# Revit family: Andreu World_Anna_SI1368
name_source: partatom
category: Furniture
revit_build: Autodesk Revit 2013 (Build: 20120221_2030(x64)
units: mm (PartAtom-declared; Revit-internal decimal feet)

## types (1)
- SI-1368
    Depth = 565 mm  [stored 1.85367 ft]
    Description = Chair with upholstered seat and backrest and solid beech wood frame. Low back, wider version.
    Front Legs Height = 435 mm  [stored 1.42717 ft]
    Height = 875 mm  [stored 2.87073 ft]
    Manufacturer = Andreu World
    Model = Anna
    Reference = SI-1368
    Seat Height = 460 mm  [stored 1.50919 ft]
    Seat Width = 470 mm
    URL = http://www.andreuworld.com
    Upholstery Material = Andreu World Fabric
    Width = 500 mm  [stored 1.64042 ft]
    Wood = Andreu World Beech

note: [stored X ft] marks values corroborated as IEEE doubles in the binary element streams (Revit-internal decimal feet)

## geometry (parser evidence)
native form markers: Blend x4, Sweep x1
no freeform markers — native parametric forms only
